# Revit family: pe-rp50_160da17_50Hz
name_source: partatom
category: 機械設備
units: mm (PartAtom-declared; Revit-internal decimal feet)

## family parameters
OmniClass タイトル = Split System Air Conditioning Units
OmniClass 番号 = 23.75.10.24.21.27.27
パーツ タイプ = 標準
ロード時にボイドで切り取り = いいえ
丸型コネクタ寸法 = 直径を使用
作業面ベース = いいえ
共有 = いいえ
常に垂直 = はい
部屋計算ポイント = はい

## types (8) — shared parameters
Depth = 700  [stored 2.29659 ft]
Height = 250  [stored 0.82021 ft]
IfcExportAs = IfcUnitaryEquipmentType
IfcExportType = AIRCONDITIONINGUNIT
OmniClassCode = 23-751024212727
RAサイズ_D = 210  [stored 0.688976 ft]
SAサイズ_D = 178  [stored 0.58399 ft]
URL = https://www.mitsubishielectric.co.jp
Uniclass2015Code = Pr_70_65_03_84
Uniclass2015Title = Split coil remote air cooled condensing units
Uniclass2015Version = Systems v1.9
ケーブルサイズ = 2 mm
サービススペース = はい
ドレン管径 = 32 mm
企業コード = 108420
冷媒管径 = 100 mm
冷媒高低圧ガス管径 = 0 mm
分類コード = 50053003123080
加湿給水管径 = 0 mm
吊り位置Y = 643  [stored 2.10958 ft]
周波数 = 50 Hz
呼称 = パッケージ形空気調和機_室内機
始動方式 = 直入
形式 = 天井吊（隠ぺい）形（両ダクト形）
推奨ブレーカー容量 = 15 A
本体マテリアル = 鋼、ペイント仕上げ、アイボリー、光沢
材質 = 溶融亜鉛メッキ鋼板
極数 = 3
機外静圧 = 50.0 Pa
法定耐用年数 = 15
消費電力 = 0 kW
消費電力_冷房 = 0 kW
消費電力_加湿器 = 0 kW
消費電力_暖房 = 0 kW
消費電力_電気ヒーター = 0 kW
相 = 1
相_電気ヒーター = 1
積算_科目 = 1 空気調和設備
符号 = PAC-CID
製品リリース年月 = 2021/5/10
製品出荷対象 = 国内
製造元 = 三菱電機株式会社
設置方法 = 天井吊(隠ぺい)形
設計冷房能力 = 0 kW
設計冷房能力_顕熱 = 0 kW
設計暖房能力 = 0 kW
説明 = 空冷ヒートホ゜ンフ゜インハ゛ータPAC 天井埋込形
負荷分類 = 3_ファン類
運転質量 = 0.00 kg
電動機出力_送風機 = 0 kW
電圧 = 200 V
電圧_電気ヒーター = 0 V
電源種別 = 一般
zero-valued in all types: 価格, 有効加湿量

## per-type parameters (varying)
| type | MAX風量 | MID風量 | MIN風量 | RAサイズ_W | SAサイズ_W | Width | モデル | 冷媒ガス管径 | 冷媒液管径 | 冷媒管径符号 | 冷房能力 | 吊り位置X | 暖房能力 | 製品質量 | 質量 | 音響パワーレベル(dB) | 音響パワーレベル（中）(dB) | 音響パワーレベル（弱）(dB) | 風量 | 風量（m3／min） | 風量（中）（m3／min） | 風量（弱）（m3／min） |
| PE-RP50DA17_50Hz | 1020.0 m³/h | 870.0 m³/h | 720.0 m³/h | 858  [stored 2.81496 ft] | 860 | 900  [stored 2.95276 ft] | PE-RP50DA17 | 13 mm | 6 mm | Ac | 5 kW | 954  [stored 3.12992 ft] | 5 kW | 27.00 kg | 32.40 kg | 56 | 53 | 51 | 1020.0 m³/h | 17 | 14.5 | 12 |
| PE-RP56DA17_50Hz | 1020.0 m³/h | 870.0 m³/h | 720.0 m³/h | 1058  [stored 3.47113 ft] | 1060  [stored 3.47769 ft] | 1100 | PE-RP56DA17 | 13 mm | 6 mm | Ac | 6 kW | 1154  [stored 3.78609 ft] | 6 kW | 27.00 kg | 32.40 kg | 57 | 54 | 53 | 1020.0 m³/h | 17 | 14.5 | 12 |
| PE-RP63DA17_50Hz | 1260.0 m³/h | 1080.0 m³/h | 870.0 m³/h | 1058  [stored 3.47113 ft] | 1060  [stored 3.47769 ft] | 1100 | PE-RP63DA17 | 16 mm | 10 mm | Bd | 7 kW | 1154  [stored 3.78609 ft] | 8 kW | 29.00 kg | 34.80 kg | 59 | 56 | 55 | 1260.0 m³/h | 21 | 18 | 14.5 |
| PE-RP71DA17_50Hz | 1260.0 m³/h | 1080.0 m³/h | 870.0 m³/h | 1358 | 1360  [stored 4.46194 ft] | 1400  [stored 4.59318 ft] | PE-RP71DA17 | 16 mm | 10 mm | Bd | 13 kW | 1454  [stored 4.77034 ft] | 14 kW | 29.00 kg | 34.80 kg | 63 | 61 | 60 | 1260.0 m³/h | 21 | 18 | 14.5 |
| PE-RP80DA17_50Hz | 1500.0 m³/h | 1260.0 m³/h | 1050.0 m³/h | 1058  [stored 3.47113 ft] | 1060  [stored 3.47769 ft] | 1100 | PE-RP80DA17 | 16 mm | 10 mm | Bd | 7 kW | 1154  [stored 3.78609 ft] | 8 kW | 29.00 kg | 34.80 kg | 59 | 56 | 55 | 1500.0 m³/h | 25 | 21 | 17.5 |
| PE-RP112DA17_50Hz | 2040.0 m³/h | 1740.0 m³/h | 1440.0 m³/h | 1358 | 1360  [stored 4.46194 ft] | 1400  [stored 4.59318 ft] | PE-RP112DA17 | 16 mm | 10 mm | Bd | 10 kW | 1454  [stored 4.77034 ft] | 11 kW | 38.00 kg | 45.60 kg | 62 | 60 | 58 | 2040.0 m³/h | 34 | 29 | 24 |
| PE-RP140DA17_50Hz | 2040.0 m³/h | 1740.0 m³/h | 1440.0 m³/h | 1358 | 1360  [stored 4.46194 ft] | 1400  [stored 4.59318 ft] | PE-RP140DA17 | 16 mm | 10 mm | Bd | 13 kW | 1454  [stored 4.77034 ft] | 14 kW | 38.00 kg | 45.60 kg | 63 | 61 | 60 | 2040.0 m³/h | 34 | 29 | 24 |
| PE-RP160DA17_50Hz | 2040.0 m³/h | 1740.0 m³/h | 1440.0 m³/h | 1358 | 1360  [stored 4.46194 ft] | 1400  [stored 4.59318 ft] | PE-RP160DA17 | 16 mm | 10 mm | Bd | 14 kW | 1454  [stored 4.77034 ft] | 16 kW | 38.00 kg | 45.60 kg | 63 | 62 | 61 | 2040.0 m³/h | 34 | 29 | 24 |

note: [stored X ft] marks values corroborated as IEEE doubles in the binary element streams (Revit-internal decimal feet)
